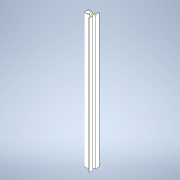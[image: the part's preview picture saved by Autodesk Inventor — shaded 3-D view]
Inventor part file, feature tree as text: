
AUTODESK INVENTOR PART (.ipt)
format: ipt  version: 2022 (Build 260153000, 153)  size: 118,784 bytes
history: native  units: in
note: dims shown in document units (in); Inventor stores cm internally (conversion verified against a paired STEP export)
features: sketch x2, extrude x1
ambient origin geometry x8: Origin, YZ Plane, XZ Plane, XY Plane, X Axis, Y Axis, Z Axis, Center Point
bodies: Solid1 (feature_tree)
feature tree (3):
  extrude  "Extrusion1"  Depth=1.4764in
  sketch  "Sketch2"  dims[d2=0.2756in d3=0.7874in d4=0.7874in d11=1.063in d12=0.2756in d14=0.1575in d16=0.2756in d18=0.1575in d19=40.5512in d20=0.0in]
  sketch  "Sketch1"  dims[d0=1.4764in d1=1.4764in]
